# Revit family: NLRS_74_PF_UN_wastafel_S8310500000_SPHINX_BCB
name_source: partatom
category: Plumbing Fixtures
revit_build: Autodesk Revit 2016 (Build: 20150220_1215(x64)
units: mm (PartAtom-declared; Revit-internal decimal feet)

## family parameters
Always vertical = Yes
Cut with Voids When Loaded = No
OmniClass Number = 23.45.00.00
OmniClass Title = Sanitary, Laundry, and Cleaning Equipment
Part Type = Normal
Room Calculation Point = No
Round Connector Dimension = Use Radius
Shared = No
Work Plane-Based = No

## types (1)
- NLRS_74_PF_UN_wastafel_S8310500000_SPHINX_BCB
    Assembly Code = 47.11
    Description = wastafel
    IfcElement = IfcFlowTerminal
    IfcExportAs = IfcSanitaryTerminalTypeEnum
    IfcExportType = SINK
    IfcTypeProduct = IfcSanitaryTerminalType
    Manufacturer = Sphinx
    NLRS_C_URL_BCB = http://bcb-online.nl
    NLRS_C_URL_product_data = http://www.sphinx.nl
    NLRS_C_breedte = 850 mm
    NLRS_C_code_EAN = 8711754407442
    NLRS_C_content_datum_gewijzigd = APR-2018
    NLRS_C_content_datum_uitgifte = APR-2018
    NLRS_C_content_provider = BouwConnect
    NLRS_C_content_versie = 2.0
    NLRS_C_diameter_in = 35 mm  [stored 0.114829 ft]
    NLRS_C_diameter_uit = 45 mm  [stored 0.147638 ft]
    NLRS_C_hoogte = 250 mm
    NLRS_C_lengte = 480 mm  [stored 1.5748 ft]
    NLRS_C_materiaal = <By Category>
    NLRS_C_revit_versie = 2016
    NLRS_C_serie = 320
    NLRS_C_type = Wastafel met kraangat en overloop
    NLRS_S_gewicht = 27.30 kg
    URL = http://www.sphinx.nl
    WFU = 0
    afvoer_radius = 23 mm

note: [stored X ft] marks values corroborated as IEEE doubles in the binary element streams (Revit-internal decimal feet)

## geometry (parser evidence)
native form markers: Blend x772, Sweep x4
no freeform markers — native parametric forms only
